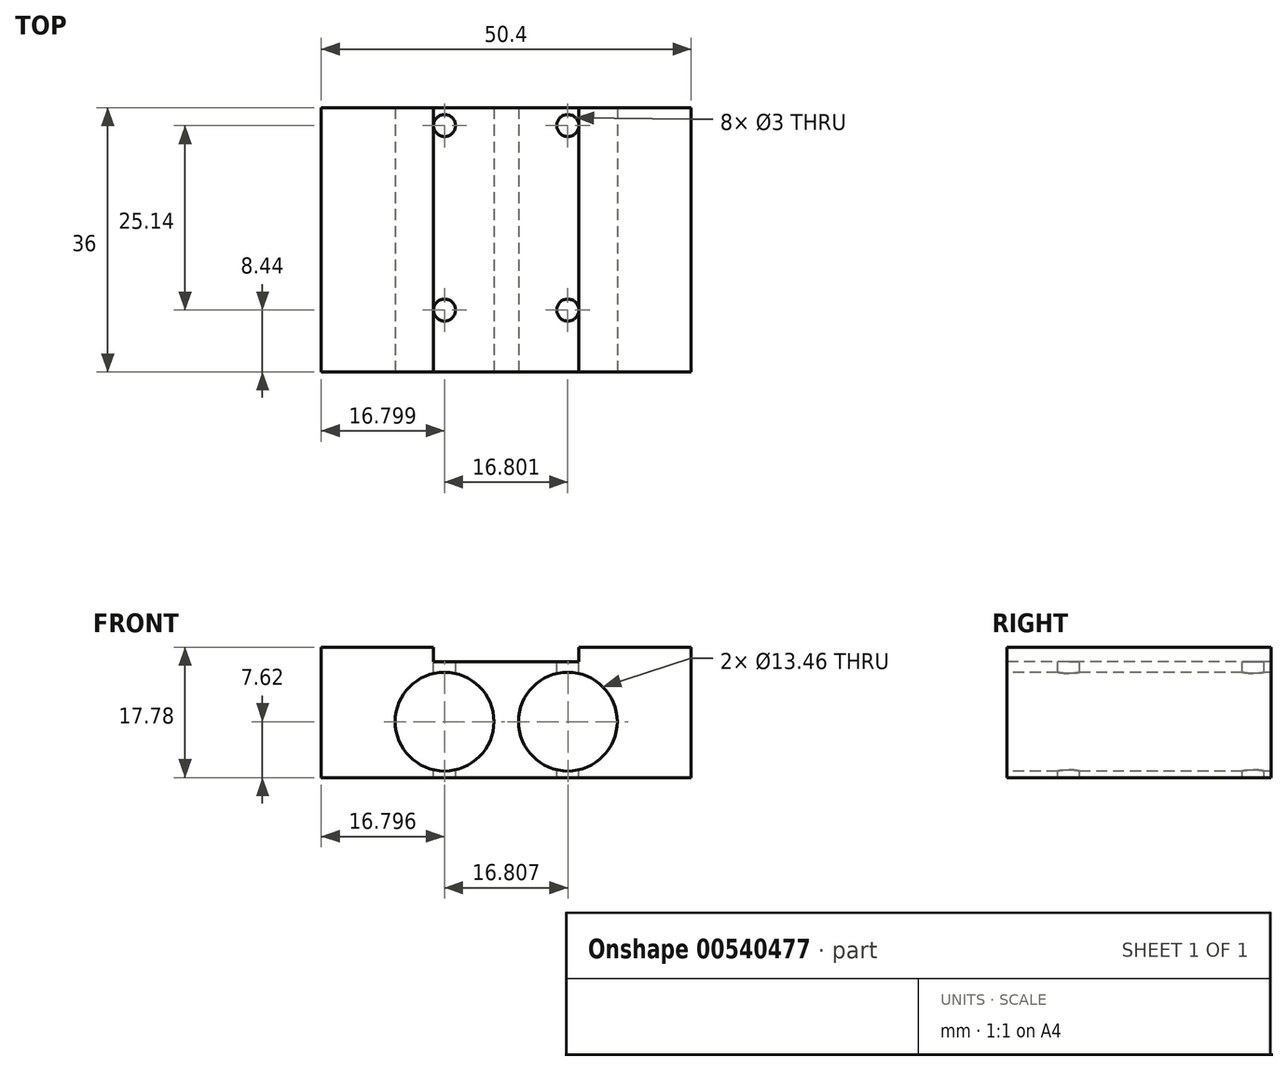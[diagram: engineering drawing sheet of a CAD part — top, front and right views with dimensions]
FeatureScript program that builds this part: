
annotation { "Feature Type Name" : "Feature", "Feature Type Description" : "" }
export const myFeature = defineFeature(function(context is Context, id is Id, definition is map)
    precondition{}
    {
        {
            var Q0;
            Q0=qCreatedBy(makeId("Top.planeOp"),FACE);
            var sketch = newSketch(context, id + "F0", { "sketchPlane" : qUnion([Q0])});
            skLineSegment(sketch, "E0.bottom", {"start": v(-25.2, 18) * mm, "end": v(25.2, 18) * mm});
            skLineSegment(sketch, "E0.top", {"start": v(-25.2, -18) * mm, "end": v(25.2, -18) * mm});
            skLineSegment(sketch, "E0.left", {"start": v(-25.2, 18) * mm, "end": v(-25.2, -18) * mm});
            skLineSegment(sketch, "E0.right", {"start": v(25.2, 18) * mm, "end": v(25.2, -18) * mm});
            skLineSegment(sketch, "E1", {"start": v(0, 18) * mm, "end": v(0, -18) * mm, "construction": true});
            skLineSegment(sketch, "E2", {"start": v(-25.2, 0) * mm, "end": v(25.2, 0) * mm, "construction": true});
            skPoint(sketch, "E3", {"position": v(0, 0) * mm});
            skPoint(sketch, "E4", {"position": v(8.4, 18) * mm});
            skLineSegment(sketch, "E5", {"start": v(8.4, 18) * mm, "end": v(8.4, -18) * mm, "construction": true});
            skPoint(sketch, "E6", {"position": v(25.2, 15.58) * mm});
            skLineSegment(sketch, "E7", {"start": v(25.2, 15.58) * mm, "end": v(-25.2, 15.58) * mm, "construction": true});
            skPoint(sketch, "E8", {"position": v(-8.4, 18) * mm});
            skLineSegment(sketch, "E9", {"start": v(-8.4, 18) * mm, "end": v(-8.4, -18) * mm, "construction": true});
            skPoint(sketch, "E10", {"position": v(25.2, -9.56) * mm});
            skLineSegment(sketch, "E11", {"start": v(25.2, -9.56) * mm, "end": v(-25.2, -9.56) * mm, "construction": true});
            skPoint(sketch, "E12", {"position": v(8.4, 15.58) * mm});
            skPoint(sketch, "E13", {"position": v(-8.4, 15.58) * mm});
            skPoint(sketch, "E14", {"position": v(-8.4, -9.56) * mm});
            skPoint(sketch, "E15", {"position": v(8.4, -9.56) * mm});
            skCircle(sketch, "E16", {"center": v(8.4, 15.58) * mm, "radius": 1.5 * mm});
            skCircle(sketch, "E17", {"center": v(-8.4, 15.58) * mm, "radius": 1.5 * mm});
            skCircle(sketch, "E18", {"center": v(-8.4, -9.56) * mm, "radius": 1.5 * mm});
            skCircle(sketch, "E19", {"center": v(8.4, -9.56) * mm, "radius": 1.5 * mm});
            skLineSegment(sketch, "E20", {"start": v(-25.2, -11.06) * mm, "end": v(25.2, -11.06) * mm, "construction": true});
            skLineSegment(sketch, "E21", {"start": v(-9.9, 18) * mm, "end": v(-9.9, -18) * mm, "construction": true});
            skLineSegment(sketch, "E22", {"start": v(9.9, 18) * mm, "end": v(9.9, -18) * mm, "construction": true});
            skLineSegment(sketch, "E23", {"start": v(-25.2, 17.08) * mm, "end": v(25.2, 17.08) * mm, "construction": true});
            skSolve(sketch);
        }
        {
            var Q0;
            Q0 = qSketchRegion(id + "F0", true);
            extrude(context, id + "F1", {"entities" : qUnion([Q0]), "oppositeDirection" : true, "depth" : 17.78 * mm, "offsetDistance" : 25 * mm});
        }
        {
            var Q0;
            Q0=makeQuery(id+"F1.opExtrude","SWEPT_FACE",FACE,{"disambiguationData":[OSD([sQuery(id+"F0.wireOp",EDGE,"E0.bottom")])]});
            var sketch = newSketch(context, id + "F2", { "sketchPlane" : qUnion([Q0])});
            skLineSegment(sketch, "E24", {"start": v(25.2, -6.35) * mm, "end": v(-25.2, -6.35) * mm, "construction": true});
            skPoint(sketch, "E25", {"position": v(8.4, -6.35) * mm});
            skPoint(sketch, "E26", {"position": v(-8.4, -6.35) * mm});
            skSolve(sketch);
        }
        {
            var Q0;
            Q0=makeQuery(id+"F1.opExtrude","SWEPT_FACE",FACE,{"disambiguationData":[OSD([sQuery(id+"F0.wireOp",EDGE,"E0.top")])]});
            var sketch = newSketch(context, id + "F3", { "sketchPlane" : qUnion([Q0])});
            skLineSegment(sketch, "E27", {"start": v(-25.2, -10.16) * mm, "end": v(25.2, -10.16) * mm, "construction": true});
            skPoint(sketch, "E28", {"position": v(-8.4, -10.16) * mm});
            skPoint(sketch, "E29", {"position": v(8.4, -10.16) * mm});
            skCircle(sketch, "E30", {"center": v(-8.4, -10.16) * mm, "radius": 6.73 * mm});
            skCircle(sketch, "E31", {"center": v(8.4, -10.16) * mm, "radius": 6.73 * mm});
            skSolve(sketch);
        }
        {
            var Q0;
            Q0 = qSketchRegion(id + "F3", true);
            extrude(context, id + "F4", {"entities" : qUnion([Q0]), "operationType" : NewBodyOperationType.REMOVE, "oppositeDirection" : true, "depth" : 63.2 * mm, "offsetDistance" : 25 * mm});
        }
        {
            var Q0;
            Q0=makeQuery(id+"F1.opExtrude","CAP_FACE",FACE,{"disambiguationData":[OSD([sQuery(id+"F0.wireOp",EDGE,"E0.bottom"),sQuery(id+"F0.wireOp",EDGE,"E0.top"),sQuery(id+"F0.wireOp",EDGE,"E0.left"),sQuery(id+"F0.wireOp",EDGE,"E0.right"),sQuery(id+"F0.wireOp",EDGE,"E16"),sQuery(id+"F0.wireOp",EDGE,"E17"),sQuery(id+"F0.wireOp",EDGE,"E18"),sQuery(id+"F0.wireOp",EDGE,"E19")])],"isStart":true});
            var sketch = newSketch(context, id + "F5", { "sketchPlane" : qUnion([Q0])});
            skLineSegment(sketch, "E32.bottom", {"start": v(-9.9, 18) * mm, "end": v(9.9, 18) * mm});
            skLineSegment(sketch, "E32.top", {"start": v(-9.9, -18) * mm, "end": v(9.9, -18) * mm});
            skLineSegment(sketch, "E32.left", {"start": v(-9.9, 18) * mm, "end": v(-9.9, -18) * mm});
            skLineSegment(sketch, "E32.right", {"start": v(9.9, 18) * mm, "end": v(9.9, -18) * mm});
            skSolve(sketch);
        }
        {
            var Q0;
            Q0 = qSketchRegion(id + "F5", true);
            extrude(context, id + "F6", {"entities" : qUnion([Q0]), "operationType" : NewBodyOperationType.REMOVE, "oppositeDirection" : true, "depth" : 2 * mm, "offsetDistance" : 25 * mm});
        }
    });
